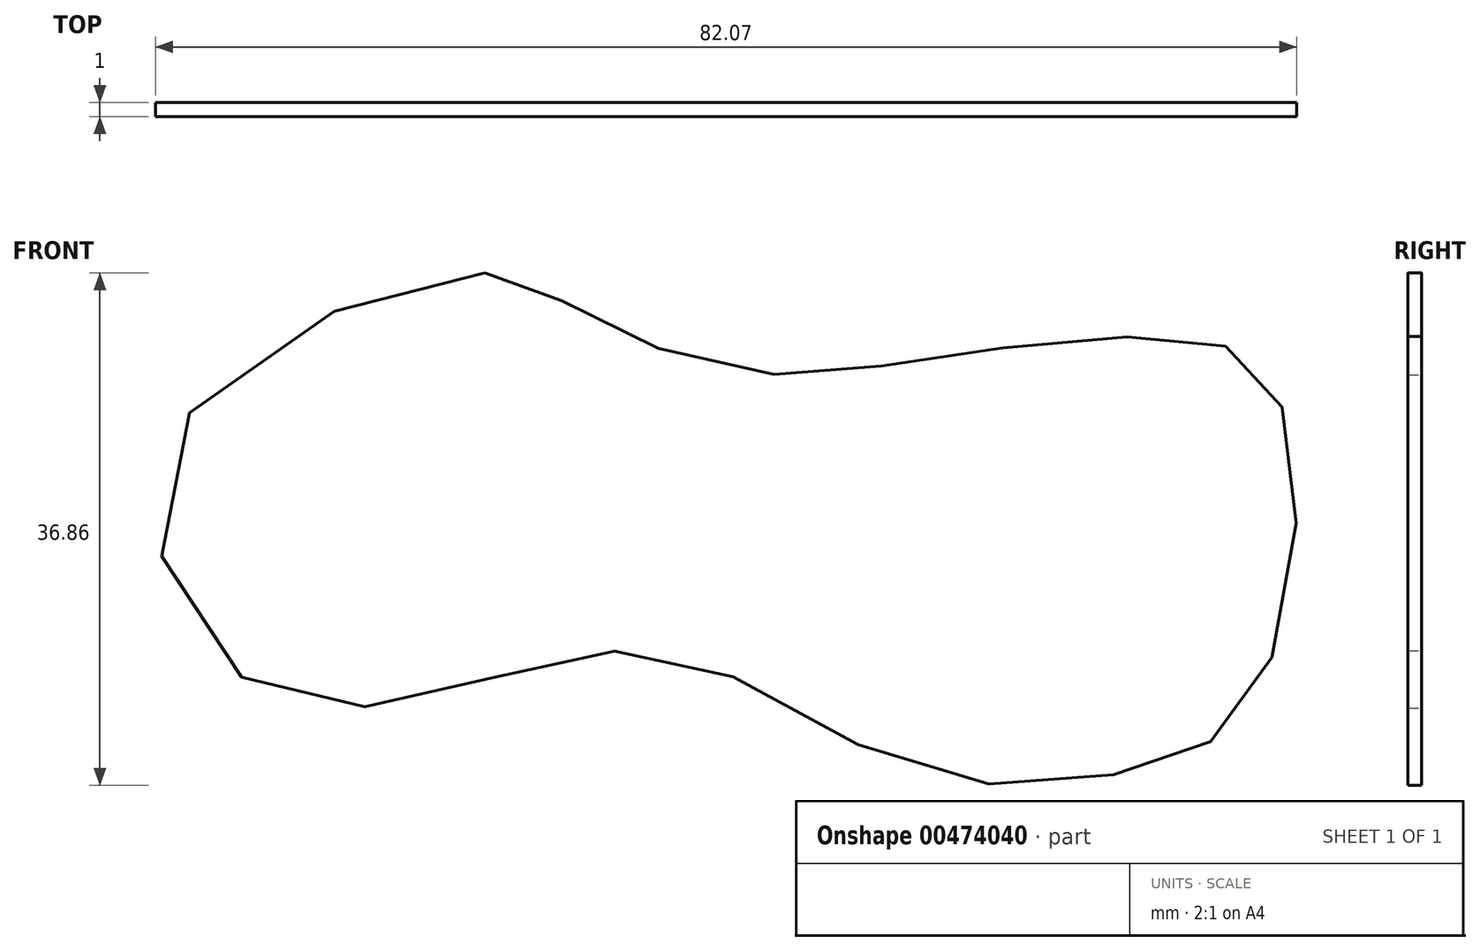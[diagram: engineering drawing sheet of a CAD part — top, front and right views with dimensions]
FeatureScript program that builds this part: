
annotation { "Feature Type Name" : "Feature", "Feature Type Description" : "" }
export const myFeature = defineFeature(function(context is Context, id is Id, definition is map)
    precondition{}
    {
        {
            var Q0;
            Q0=qCreatedBy(makeId("Front.planeOp"),FACE);
            var sketch = newSketch(context, id + "F0", { "sketchPlane" : qUnion([Q0])});
            skFitSpline(sketch, "E0", {"points": [v(-14.1, 25.23) * mm, v(-36.74, 12.95) * mm, v(-30.6, -4.5) * mm, v(-14.3, -4.12) * mm, v(0, -2.4) * mm, v(17.36, -10.65) * mm, v(32.9, -10.46) * mm, v(40.96, -5.66) * mm, v(44.22, 10.65) * mm, v(40.77, 19.09) * mm, v(32.13, 20.62) * mm, v(16.6, 18.9) * mm, v(4.7, 18.13) * mm, v(-7.77, 22.73) * mm, v(-14.1, 25.23) * mm]});
            skSolve(sketch);
        }
        {
            var Q0;
            Q0 = qSketchRegion(id + "F0", true);
            extrude(context, id + "F1", {"entities" : qUnion([Q0]), "depth" : 1 * mm});
        }
    });
